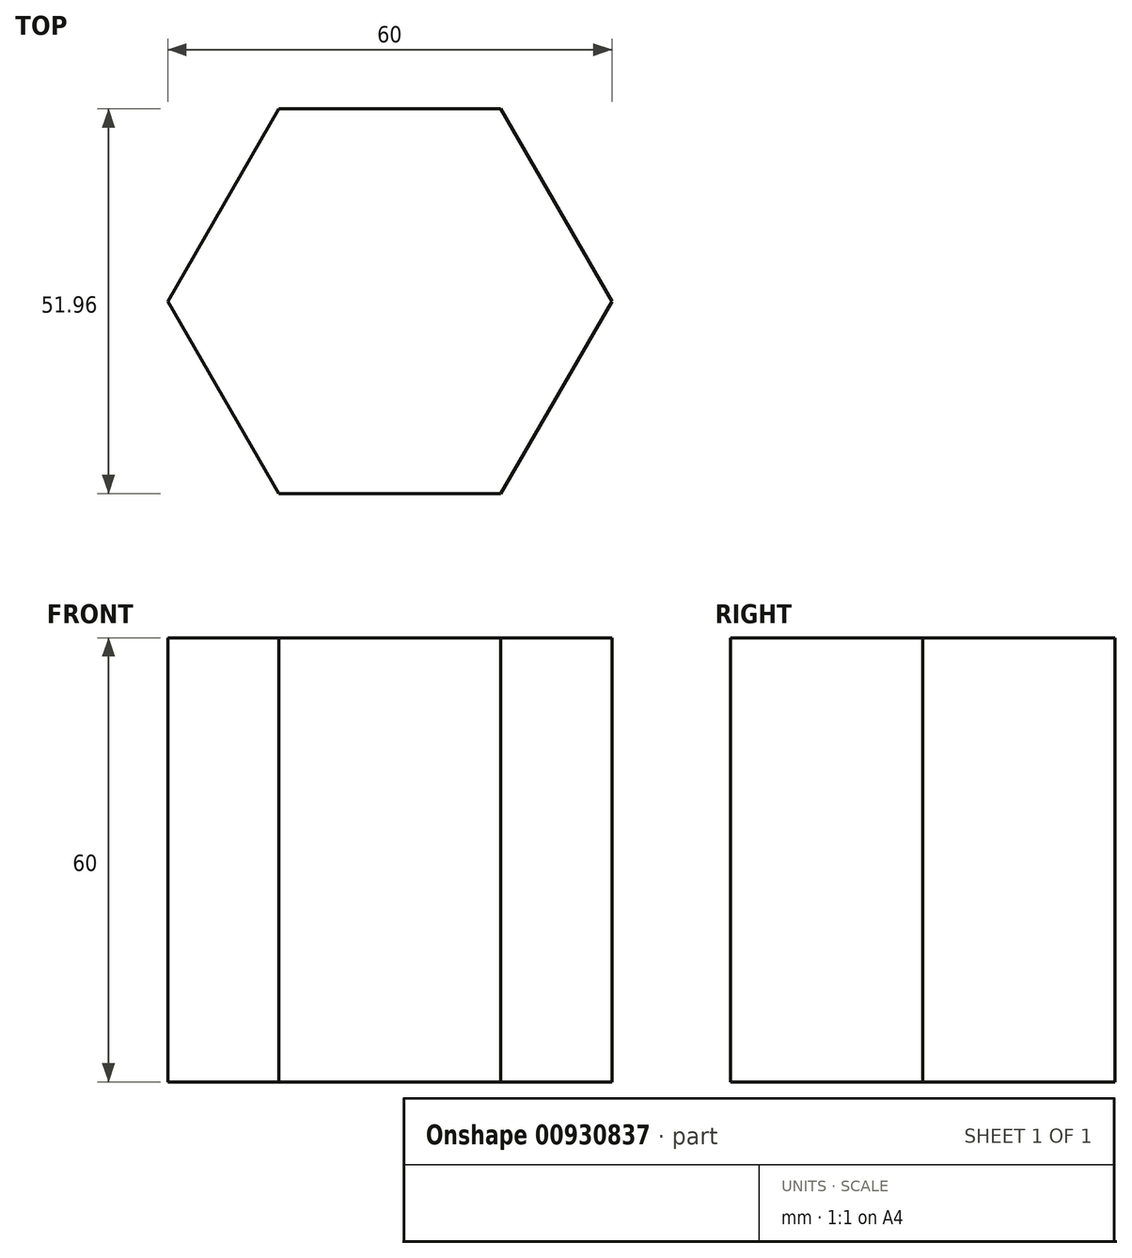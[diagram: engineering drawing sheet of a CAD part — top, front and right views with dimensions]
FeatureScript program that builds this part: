
annotation { "Feature Type Name" : "Feature", "Feature Type Description" : "" }
export const myFeature = defineFeature(function(context is Context, id is Id, definition is map)
    precondition{}
    {
        {
            var Q0;
            Q0=qCreatedBy(makeId("Top.planeOp"),FACE);
            var sketch = newSketch(context, id + "F0", { "sketchPlane" : qUnion([Q0])});
            skCircle(sketch, "E0.cCircle", {"center": v(0, 0) * mm, "radius": 30 * mm, "construction": true});
            skLineSegment(sketch, "E0.0", {"start": v(30, 0) * mm, "end": v(15, -25.98) * mm});
            skLineSegment(sketch, "E0.1", {"start": v(15, -25.98) * mm, "end": v(-15, -25.98) * mm});
            skLineSegment(sketch, "E0.2", {"start": v(-15, -25.98) * mm, "end": v(-30, 0) * mm});
            skLineSegment(sketch, "E0.3", {"start": v(-30, 0) * mm, "end": v(-15, 25.98) * mm});
            skLineSegment(sketch, "E0.4", {"start": v(-15, 25.98) * mm, "end": v(15, 25.98) * mm});
            skLineSegment(sketch, "E0.5", {"start": v(15, 25.98) * mm, "end": v(30, 0) * mm});
            skSolve(sketch);
        }
        {
            var Q0;
            Q0 = qSketchRegion(id + "F0", true);
            extrude(context, id + "F1", {"entities" : qUnion([Q0]), "depth" : 60 * mm, "offsetDistance" : 25 * mm});
        }
    });
